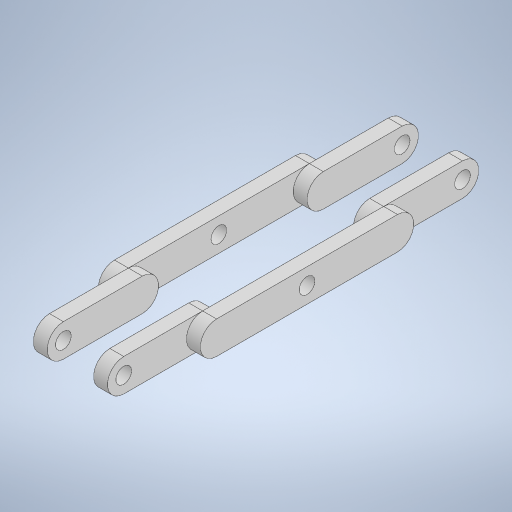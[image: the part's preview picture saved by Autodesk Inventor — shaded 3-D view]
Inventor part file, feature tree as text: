
AUTODESK INVENTOR PART (.ipt)
format: ipt  version: 2024.3 (Build 283343000, 343)  size: 306,176 bytes
history: native  units: mm
features: extrude x4, sketch x3, hole x2
ambient origin geometry x8: Origin, YZ Plane, XZ Plane, XY Plane, X Axis, Y Axis, Z Axis, Center Point
bodies: Body1 (feature_tree)
feature tree (9):
  sketch  "Sketch1"  dims[d17=5.0mm d18=80.0mm]
  extrude  "Extrusión3"  Depth=80.0mm
  extrude  "Extrusión4"  Depth=7.0mm
  extrude  "Extrusión5"  Depth=16.0mm TaperAngle=0.0deg
  extrude  "Extrusión6"  Depth=8.0mm
  hole  "Agujero1"  [1 undecoded]
  hole  "Agujero2"  [1 undecoded]
  sketch  "Boceto2"  dims[d19=3.0mm d20=7.0mm]
  sketch  "Boceto3"  dims[d21=22.0mm d22=0.0mm d23=16.0mm d24=0.0mm d25=3.4mm d26=6.0mm d27=6.3mm d28=2.0mm d29=90.0deg d30=8.0mm d31=20.594885mm d32=39.0mm d33=16.0mm d34=0.0mm d35=10.0mm d36=0.0mm d37=3.4mm d38=6.0mm d39=6.3mm d40=2.0mm d41=90.0deg d42=8.0mm d43=20.594885mm]
note: 2 required parameter values undecoded (feature->parameter linkage not recoverable at this tier; creation-order binding heuristic only, values carry confidence <= 0.55)
